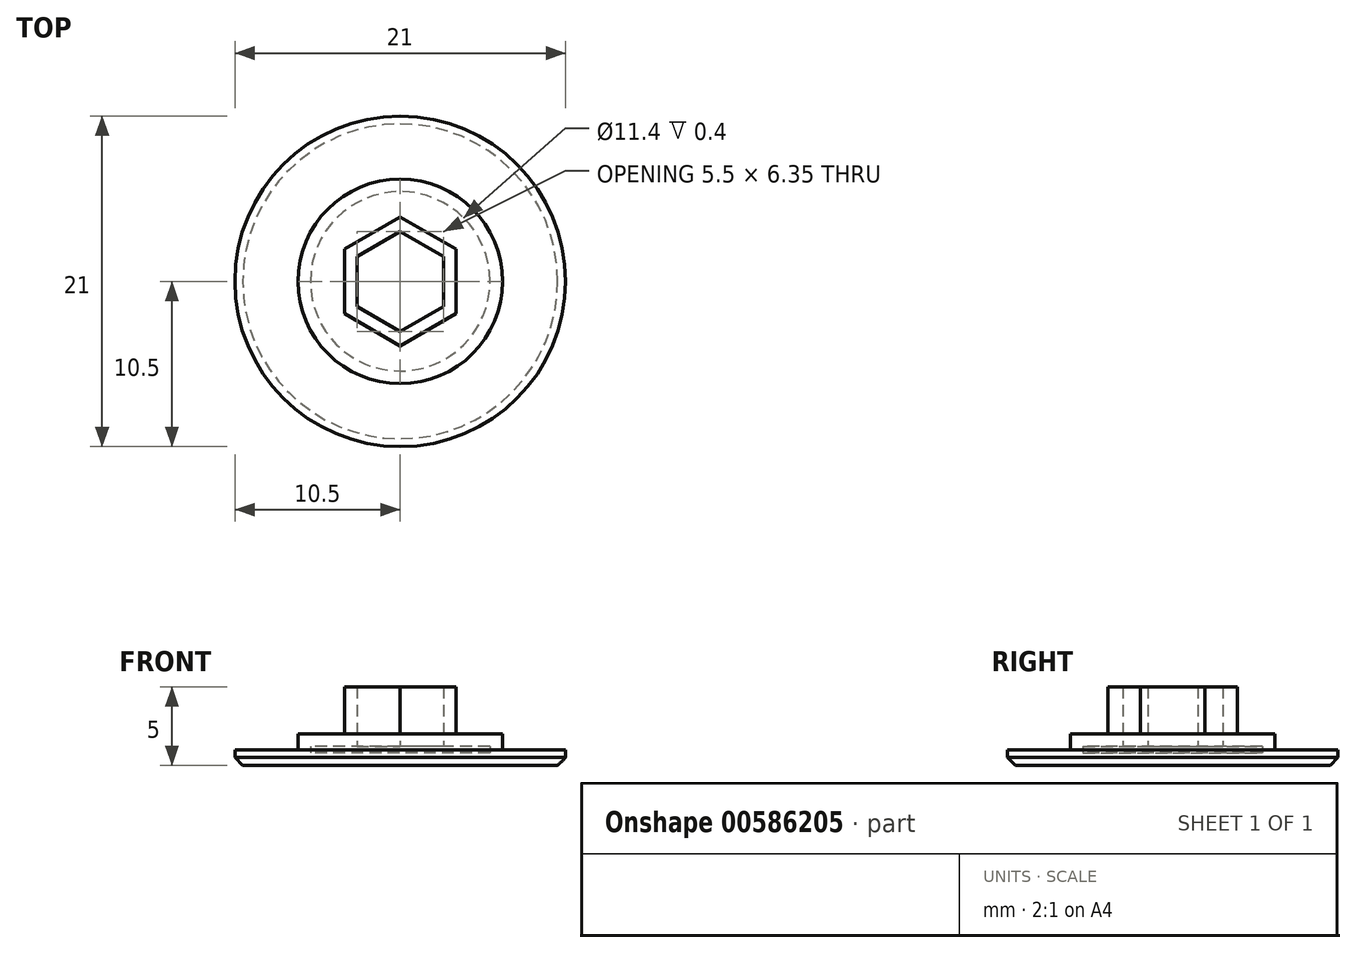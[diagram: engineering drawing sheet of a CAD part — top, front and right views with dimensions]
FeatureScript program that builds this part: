
annotation { "Feature Type Name" : "Feature", "Feature Type Description" : "" }
export const myFeature = defineFeature(function(context is Context, id is Id, definition is map)
    precondition{}
    {
        {
            var Q0;
            Q0=qCreatedBy(makeId("Top.planeOp"),FACE);
            var sketch = newSketch(context, id + "F0", { "sketchPlane" : qUnion([Q0]), "disableImprinting" : false});
            skCircle(sketch, "E0", {"center": v(0, 0) * mm, "radius": 10.5 * mm});
            skSolve(sketch);
        }
        {
            var Q0;
            Q0=makeQuery(id+"F0.imprint","IMPRINT",FACE,{"disambiguationData":[TD([[makeQuery(id+"F0.imprint","IMPRINT",EDGE,{"derivedFrom":sQuery(id+"F0.wireOp",EDGE,"E0")}),1.0]])]});
            extrude(context, id + "F1", {"entities" : qUnion([Q0]), "depth" : 1 * mm, "offsetDistance" : 25 * mm});
        }
        {
            var Q0;
            {var subQ0=sQuery(id+"F0.wireOp",EDGE,"E0");Q0=makeQuery(id+"FCE4xjLwlJGgTYo_1.boolean.opBoolean","SPLIT",FACE,{"disambiguationData":[TD([makeQuery(id+"F1.opExtrude","SWEPT_FACE",FACE,{"disambiguationData":[OSD([subQ0])]})])],"derivedFrom":makeQuery(id+"F1.opExtrude","CAP_FACE",FACE,{"disambiguationData":[OSD([subQ0])],"isStart":false})});}
            var sketch = newSketch(context, id + "F2", { "sketchPlane" : qUnion([Q0]), "disableImprinting" : false});
            skCircle(sketch, "E1", {"center": v(0, 0) * mm, "radius": 6.5 * mm});
            skSolve(sketch);
        }
        {
            var Q0;
            Q0=makeQuery(id+"F2.imprint","IMPRINT",FACE,{"disambiguationData":[TD([[makeQuery(id+"F2.imprint","IMPRINT",EDGE,{"derivedFrom":sQuery(id+"F2.wireOp",EDGE,"E1")}),1.0]])]});
            extrude(context, id + "F3", {"entities" : qUnion([Q0]), "operationType" : NewBodyOperationType.ADD, "depth" : 1 * mm, "offsetDistance" : 25 * mm});
        }
        {
            var Q0;
            Q0=makeQuery(id+"F3.opExtrude","CAP_FACE",FACE,{"disambiguationData":[OSD([sQuery(id+"F2.wireOp",EDGE,"E1")])],"isStart":false});
            var sketch = newSketch(context, id + "F4", { "sketchPlane" : qUnion([Q0])});
            skCircle(sketch, "E2.cCircle", {"center": v(0, 0) * mm, "radius": 4.1 * mm, "construction": true});
            skLineSegment(sketch, "E2.0", {"start": v(0, 4.1) * mm, "end": v(3.55, 2.05) * mm});
            skLineSegment(sketch, "E2.1", {"start": v(3.55, 2.05) * mm, "end": v(3.55, -2.05) * mm});
            skLineSegment(sketch, "E2.2", {"start": v(3.55, -2.05) * mm, "end": v(0, -4.1) * mm});
            skLineSegment(sketch, "E2.3", {"start": v(0, -4.1) * mm, "end": v(-3.55, -2.05) * mm});
            skLineSegment(sketch, "E2.4", {"start": v(-3.55, -2.05) * mm, "end": v(-3.55, 2.05) * mm});
            skLineSegment(sketch, "E2.5", {"start": v(-3.55, 2.05) * mm, "end": v(0, 4.1) * mm});
            skSolve(sketch);
        }
        {
            var Q0;
            Q0=makeQuery(id+"F4.imprint","IMPRINT",FACE,{"disambiguationData":[TD([[makeQuery(id+"F4.imprint","IMPRINT",EDGE,{"derivedFrom":sQuery(id+"F4.wireOp",EDGE,"E2.0")}),-1.0]])]});
            extrude(context, id + "F5", {"entities" : qUnion([Q0]), "operationType" : NewBodyOperationType.ADD, "depth" : 3 * mm, "offsetDistance" : 25 * mm});
        }
        {
            var Q0;
            Q0=makeQuery(id+"F5.opExtrude","CAP_FACE",FACE,{"disambiguationData":[OSD([sQuery(id+"F4.wireOp",EDGE,"E2.0"),sQuery(id+"F4.wireOp",EDGE,"E2.1"),sQuery(id+"F4.wireOp",EDGE,"E2.2"),sQuery(id+"F4.wireOp",EDGE,"E2.3"),sQuery(id+"F4.wireOp",EDGE,"E2.4"),sQuery(id+"F4.wireOp",EDGE,"E2.5")])],"isStart":false});
            shell(context, id + "F6", {"entities" : qUnion([Q0]), "thickness" : .8 * mm});
        }
        {
            var Q0;
            Q0=makeQuery(id+"F1.opExtrude","CAP_EDGE",EDGE,{"disambiguationData":[OSD([sQuery(id+"F0.wireOp",EDGE,"E0")])],"isStart":true});
            chamfer(context, id + "F7", {"entities" : qUnion([Q0]), "width" : .5 * mm, "tangentPropagation" : true});
        }
    });
